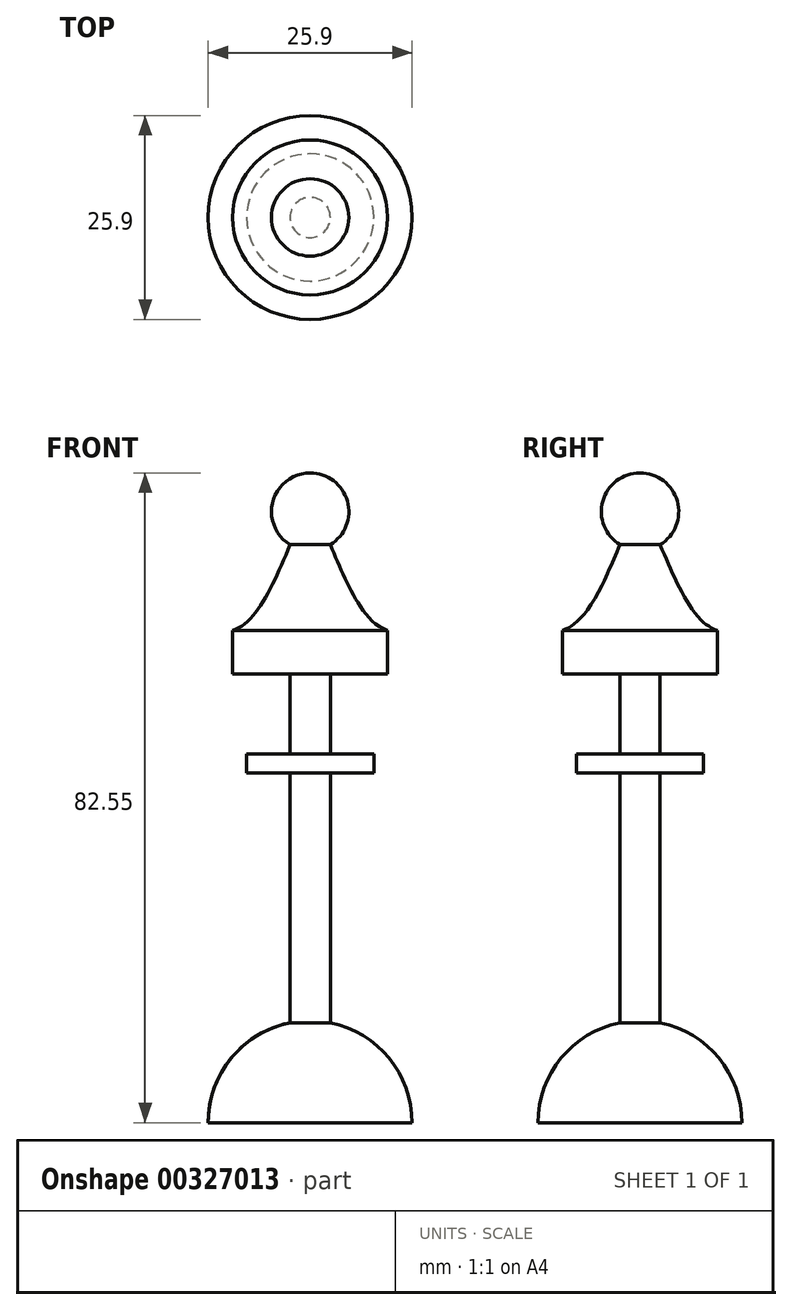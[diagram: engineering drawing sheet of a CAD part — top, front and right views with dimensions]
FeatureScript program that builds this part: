
annotation { "Feature Type Name" : "Feature", "Feature Type Description" : "" }
export const myFeature = defineFeature(function(context is Context, id is Id, definition is map)
    precondition{}
    {
        {
            var Q0;
            Q0=qCreatedBy(makeId("Front.planeOp"),FACE);
            var sketch = newSketch(context, id + "F0", { "sketchPlane" : qUnion([Q0])});
            skLineSegment(sketch, "E0", {"start": v(0, -50.94) * mm, "end": v(-12.95, -50.94) * mm});
            skArc(sketch, "E1", {"start": v(-2.55, -38.24) * mm, "mid": v(-10.02, -42.73) * mm, "end": v(-12.95, -50.94) * mm});
            skLineSegment(sketch, "E2", {"start": v(0, -50.94) * mm, "end": v(0, 44.33) * mm});
            skLineSegment(sketch, "E3", {"start": v(-2.55, -6.5) * mm, "end": v(-8.08, -6.5) * mm});
            skLineSegment(sketch, "E4", {"start": v(-8.08, -6.5) * mm, "end": v(-8.08, -4.08) * mm});
            skLineSegment(sketch, "E5", {"start": v(-8.08, -4.08) * mm, "end": v(-2.55, -4.08) * mm});
            skLineSegment(sketch, "E6", {"start": v(0, -4.08) * mm, "end": v(0, 6.03) * mm});
            skLineSegment(sketch, "E7", {"start": v(-2.55, 6.03) * mm, "end": v(-9.84, 6.03) * mm});
            skLineSegment(sketch, "E8", {"start": v(-9.84, 6.03) * mm, "end": v(-9.84, 11.6) * mm});
            skLineSegment(sketch, "E9", {"start": v(-2.55, -6.5) * mm, "end": v(-2.55, -38.24) * mm});
            skLineSegment(sketch, "E10", {"start": v(-2.55, -4.08) * mm, "end": v(-2.55, 6.03) * mm});
            skArc(sketch, "E11", {"start": v(0, 31.6) * mm, "mid": v(-4.73, 28.02) * mm, "end": v(-2.55, 22.5) * mm});
            skFitSpline(sketch, "E12", {"points": [v(-2.55, 22.5) * mm, v(-9.84, 11.6) * mm, v(-20.1, 15.97) * mm], "startDerivative": vector(-12.1, -28.74) * mm, "endDerivative": vector(-23.16, 16.3) * mm});
            skPoint(sketch, "E13.end.orphan", {"position": v(0, 11.6) * mm});
            skPoint(sketch, "E14.orphan", {"position": v(0, -6.5) * mm});
            skLineSegment(sketch, "E15", {"start": v(-9.84, 11.6) * mm, "end": v(0, 11.6) * mm});
            skLineSegment(sketch, "E16", {"start": v(-2.55, 6.03) * mm, "end": v(0, 6.03) * mm});
            skLineSegment(sketch, "E17", {"start": v(-2.55, -4.08) * mm, "end": v(0, -4.08) * mm});
            skLineSegment(sketch, "E18", {"start": v(-2.55, -6.5) * mm, "end": v(0, -6.5) * mm});
            skSolve(sketch);
        }
        {
            var Q0;
            Q0 = qSketchRegion(id + "F0", true);
            var Q1;
            Q1=sQuery(id+"F0.wireOp",EDGE,"E2");
            revolve(context, id + "F1", {"entities" : qUnion([Q0]), "axis" : qUnion([Q1]), "revolveType" : RevolveType.FULL});
        }
    });
